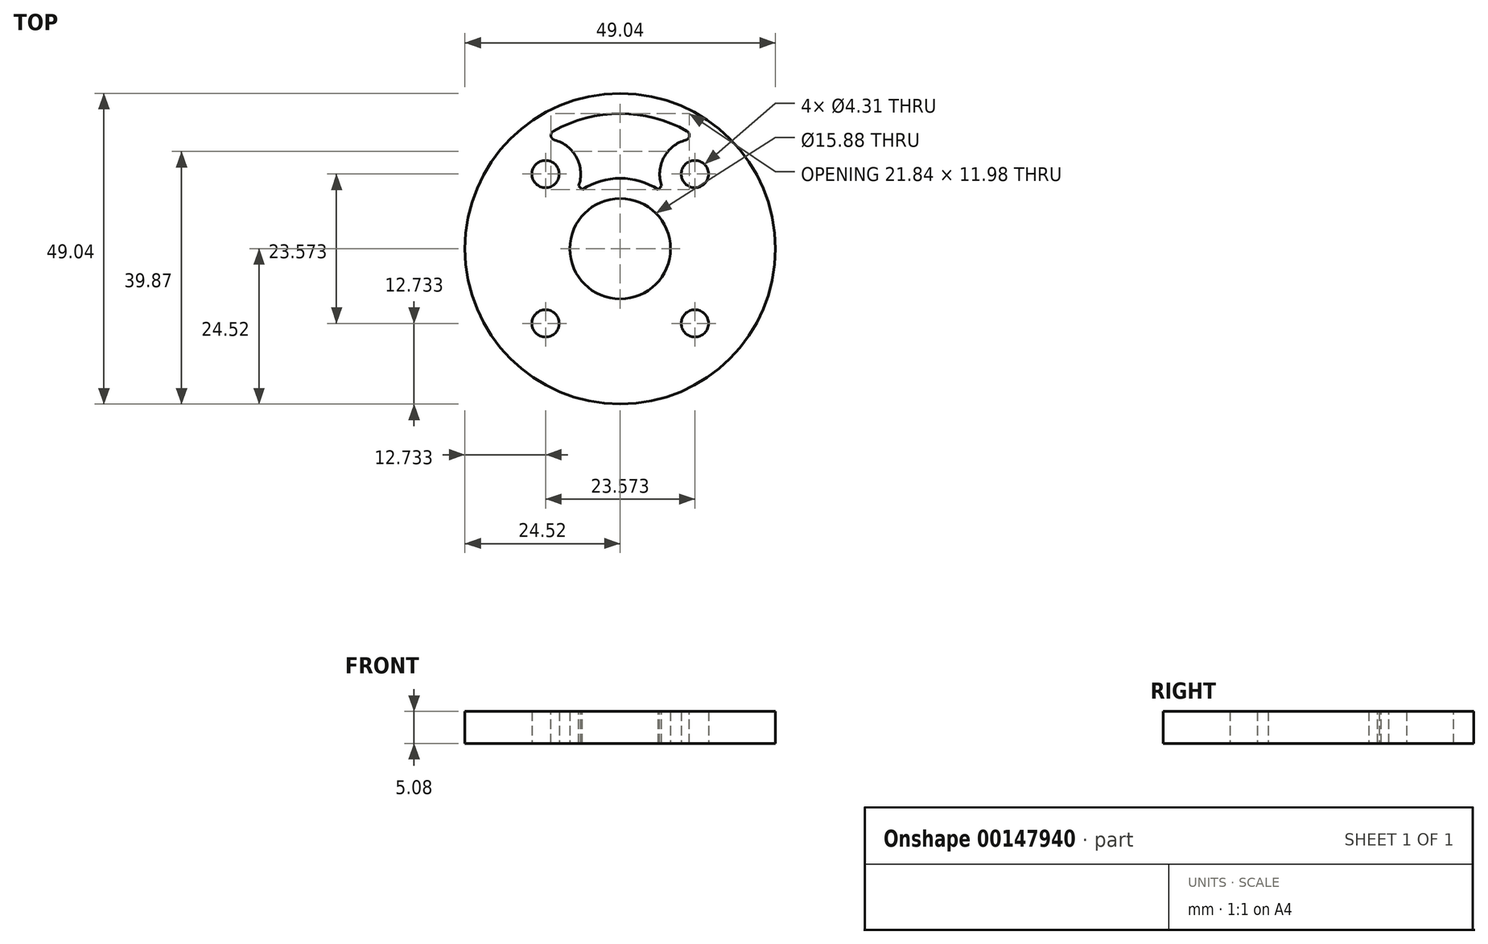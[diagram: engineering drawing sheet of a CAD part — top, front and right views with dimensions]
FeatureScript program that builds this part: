
annotation { "Feature Type Name" : "Feature", "Feature Type Description" : "" }
export const myFeature = defineFeature(function(context is Context, id is Id, definition is map)
    precondition{}
    {
        {
            var Q0;
            Q0=qCreatedBy(makeId("Top.planeOp"),FACE);
            var sketch = newSketch(context, id + "F0", { "sketchPlane" : qUnion([Q0])});
            skCircle(sketch, "E0", {"center": v(0, 0) * mm, "radius": 24.52 * mm});
            skCircle(sketch, "E1", {"center": v(0, 0) * mm, "radius": 7.94 * mm});
            skLineSegment(sketch, "E2.bottom", {"start": v(-11.79, 11.79) * mm, "end": v(11.79, 11.79) * mm, "construction": true});
            skLineSegment(sketch, "E2.top", {"start": v(-11.79, -11.79) * mm, "end": v(11.79, -11.79) * mm, "construction": true});
            skLineSegment(sketch, "E2.left", {"start": v(-11.79, 11.79) * mm, "end": v(-11.79, -11.79) * mm, "construction": true});
            skLineSegment(sketch, "E2.right", {"start": v(11.79, 11.79) * mm, "end": v(11.79, -11.79) * mm, "construction": true});
            skCircle(sketch, "E3", {"center": v(-11.79, 11.79) * mm, "radius": 7.85 * mm, "construction": true});
            skCircle(sketch, "E4", {"center": v(11.79, 11.79) * mm, "radius": 2.15 * mm});
            skCircle(sketch, "E5", {"center": v(-11.79, 11.79) * mm, "radius": 2.15 * mm});
            skCircle(sketch, "E6", {"center": v(-11.79, -11.79) * mm, "radius": 2.15 * mm});
            skCircle(sketch, "E7", {"center": v(11.79, -11.79) * mm, "radius": 2.15 * mm});
            skCircle(sketch, "E8", {"center": v(-11.79, -11.79) * mm, "radius": 3.97 * mm, "construction": true});
            skCircle(sketch, "E9", {"center": v(11.79, 11.79) * mm, "radius": 3.97 * mm, "construction": true});
            skSolve(sketch);
        }
        {
            var Q0;
            Q0=qSketchRegion(id+"F0",true);
            extrude(context, id + "F1", {"entities" : qUnion([Q0]), "depth" : 5.08 * mm});
        }
        {
            var Q0;
            Q0=makeQuery(id+"F1.opExtrude","CAP_FACE",FACE,{"disambiguationData":[OSD([sQuery(id+"F0.wireOp",EDGE,"E0"),sQuery(id+"F0.wireOp",EDGE,"E1"),sQuery(id+"F0.wireOp",EDGE,"E4"),sQuery(id+"F0.wireOp",EDGE,"E5"),sQuery(id+"F0.wireOp",EDGE,"E6"),sQuery(id+"F0.wireOp",EDGE,"E7")])],"isStart":false});
            var sketch = newSketch(context, id + "F2", { "sketchPlane" : qUnion([Q0])});
            skArc(sketch, "E10", {"start": v(-6.55, 9.92) * mm, "mid": v(-7.46, 15.27) * mm, "end": v(-12.5, 17.3) * mm});
            skArc(sketch, "E11", {"start": v(12.5, 17.3) * mm, "mid": v(7.46, 15.27) * mm, "end": v(6.55, 9.92) * mm});
            skArc(sketch, "E12", {"start": v(12.5, 17.3) * mm, "mid": v(0, 21.34) * mm, "end": v(-12.5, 17.3) * mm});
            skArc(sketch, "E13", {"start": v(6, 9.36) * mm, "mid": v(0, 11.11) * mm, "end": v(-6, 9.36) * mm});
            skLineSegment(sketch, "E14.bottom", {"start": v(-9.92, 6.55) * mm, "end": v(-6.55, 9.92) * mm, "construction": true});
            skLineSegment(sketch, "E14.top", {"start": v(-9.36, 6) * mm, "end": v(-6, 9.36) * mm, "construction": true});
            skLineSegment(sketch, "E14.left", {"start": v(-9.92, 6.55) * mm, "end": v(-9.36, 6) * mm, "construction": true});
            skLineSegment(sketch, "E14.right", {"start": v(-6.55, 9.92) * mm, "end": v(-6, 9.36) * mm});
            skLineSegment(sketch, "E15.bottom", {"start": v(9.92, 6.55) * mm, "end": v(6.55, 9.92) * mm, "construction": true});
            skLineSegment(sketch, "E15.top", {"start": v(9.36, 6) * mm, "end": v(6, 9.36) * mm, "construction": true});
            skLineSegment(sketch, "E15.left", {"start": v(9.92, 6.55) * mm, "end": v(9.36, 6) * mm, "construction": true});
            skLineSegment(sketch, "E15.right", {"start": v(6.55, 9.92) * mm, "end": v(6, 9.36) * mm});
            skLineSegment(sketch, "E16", {"start": v(-8.24, 8.24) * mm, "end": v(-11.79, 11.79) * mm, "construction": true});
            skLineSegment(sketch, "E17", {"start": v(-7.68, 7.68) * mm, "end": v(0, 0) * mm, "construction": true});
            skLineSegment(sketch, "E18", {"start": v(0, 0) * mm, "end": v(7.68, 7.68) * mm, "construction": true});
            skLineSegment(sketch, "E19", {"start": v(8.24, 8.24) * mm, "end": v(11.79, 11.79) * mm, "construction": true});
            skSolve(sketch);
        }
        {
            var Q0;
            Q0=makeQuery(id+"F2.imprint","IMPRINT",FACE,{"disambiguationData":[TD([[makeQuery(id+"F2.imprint","IMPRINT",EDGE,{"derivedFrom":sQuery(id+"F2.wireOp",EDGE,"E10")}),-1.0]])]});
            var Q1;
            Q1=makeQuery(id+"F1.opExtrude","CAP_FACE",FACE,{"disambiguationData":[OSD([sQuery(id+"F0.wireOp",EDGE,"E0"),sQuery(id+"F0.wireOp",EDGE,"E1"),sQuery(id+"F0.wireOp",EDGE,"E4"),sQuery(id+"F0.wireOp",EDGE,"E5"),sQuery(id+"F0.wireOp",EDGE,"E6"),sQuery(id+"F0.wireOp",EDGE,"E7")])],"isStart":true});
            extrude(context, id + "F3", {"entities" : qUnion([Q0]), "operationType" : NewBodyOperationType.REMOVE, "endBound" : BoundingType.UP_TO_SURFACE, "oppositeDirection" : true, "endBoundEntityFace" : qUnion([Q1]), "depth" : 25.4 * mm});
        }
        {
            var Q0;
            Q0=makeQuery(id+"F6MqURjXbY15YYN_1.1.F3.boolean.opBoolean","COPY",EDGE,{"derivedFrom":makeQuery(id+"F6MqURjXbY15YYN_1.1.F3.opExtrude","SWEPT_EDGE",EDGE,{"disambiguationData":[OSD([sQuery(id+"F2.wireOp",EDGE,"E10"),sQuery(id+"F2.wireOp",EDGE,"E12")])]})});
            var Q1;
            Q1=makeQuery(id+"F6MqURjXbY15YYN_1.1.F3.boolean.opBoolean","COPY",EDGE,{"derivedFrom":makeQuery(id+"F6MqURjXbY15YYN_1.1.F3.opExtrude","SWEPT_EDGE",EDGE,{"disambiguationData":[OSD([sQuery(id+"F2.wireOp",EDGE,"E11"),sQuery(id+"F2.wireOp",EDGE,"E12")])]})});
            var Q2;
            Q2=makeQuery(id+"F6MqURjXbY15YYN_1.2.F3.boolean.opBoolean","COPY",EDGE,{"derivedFrom":makeQuery(id+"F6MqURjXbY15YYN_1.2.F3.opExtrude","SWEPT_EDGE",EDGE,{"disambiguationData":[OSD([sQuery(id+"F2.wireOp",EDGE,"E10"),sQuery(id+"F2.wireOp",EDGE,"E12")])]})});
            var Q3;
            Q3=makeQuery(id+"F6MqURjXbY15YYN_1.2.F3.boolean.opBoolean","COPY",EDGE,{"derivedFrom":makeQuery(id+"F6MqURjXbY15YYN_1.2.F3.opExtrude","SWEPT_EDGE",EDGE,{"disambiguationData":[OSD([sQuery(id+"F2.wireOp",EDGE,"E11"),sQuery(id+"F2.wireOp",EDGE,"E12")])]})});
            var Q4;
            Q4=makeQuery(id+"F6MqURjXbY15YYN_1.3.F3.boolean.opBoolean","COPY",EDGE,{"derivedFrom":makeQuery(id+"F6MqURjXbY15YYN_1.3.F3.opExtrude","SWEPT_EDGE",EDGE,{"disambiguationData":[OSD([sQuery(id+"F2.wireOp",EDGE,"E10"),sQuery(id+"F2.wireOp",EDGE,"E12")])]})});
            var Q5;
            Q5=makeQuery(id+"F6MqURjXbY15YYN_1.3.F3.boolean.opBoolean","COPY",EDGE,{"derivedFrom":makeQuery(id+"F6MqURjXbY15YYN_1.3.F3.opExtrude","SWEPT_EDGE",EDGE,{"disambiguationData":[OSD([sQuery(id+"F2.wireOp",EDGE,"E11"),sQuery(id+"F2.wireOp",EDGE,"E12")])]})});
            var Q6;
            Q6=makeQuery(id+"F3.boolean.opBoolean","COPY",EDGE,{"derivedFrom":makeQuery(id+"F3.opExtrude","SWEPT_EDGE",EDGE,{"disambiguationData":[OSD([sQuery(id+"F2.wireOp",EDGE,"E10"),sQuery(id+"F2.wireOp",EDGE,"E12")])]})});
            var Q7;
            Q7=makeQuery(id+"F3.boolean.opBoolean","COPY",EDGE,{"derivedFrom":makeQuery(id+"F3.opExtrude","SWEPT_EDGE",EDGE,{"disambiguationData":[OSD([sQuery(id+"F2.wireOp",EDGE,"E11"),sQuery(id+"F2.wireOp",EDGE,"E12")])]})});
            fillet(context, id + "F4", {"entities" : qUnion([Q0, Q1, Q2, Q3, Q4, Q5, Q6, Q7]), "radius" : 0.76 * mm, "tangentPropagation" : true, "allowEdgeOverflow" : false});
        }
    });
